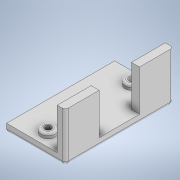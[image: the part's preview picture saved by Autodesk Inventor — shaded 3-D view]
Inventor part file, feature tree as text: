
AUTODESK INVENTOR PART (.ipt)
format: ipt  version: 2020 (Build 240168000, 168)  size: 183,296 bytes
history: native  units: in
note: dims shown in document units (in); Inventor stores cm internally (conversion verified against a paired STEP export)
features: extrude x5, sketch x4, fillet x2
ambient origin geometry x8: Origin, YZ Plane, XZ Plane, XY Plane, X Axis, Y Axis, Z Axis, Center Point
bodies: Solid1 (feature_tree)
feature tree (11):
  extrude  "Extrusion1"  Depth=2.6378in
  extrude  "Extrusion2"  Depth=0.1969in
  extrude  "Extrusion3"  Depth=0.1969in
  extrude  "Extrusion4"  Depth=1.0in TaperAngle=0.0deg
  extrude  "Extrusion5"  Depth=0.0197in
  fillet  "Fillet1"  Radius=0.3346in
  fillet  "Fillet2"  Radius=0.3346in
  sketch  "Sketch1"  dims[d0=1.4331in d1=2.6378in]
  sketch  "Sketch2"  dims[d2=0.1969in d3=0.0in d4=0.1969in]
  sketch  "Sketch3"  dims[d5=0.8268in d6=0.1969in]
  sketch  "Sketch4"  dims[d7=0.8268in d8=1.0in d9=0.0in d10=0.3346in d11=0.3346in d12=0.3346in d13=0.1181in d14=0.0in d15=0.2362in d16=0.2362in d17=0.1181in d18=0.0in d19=0.1575in d21=0.1575in d22=0.5906in d23=0.0in d24=0.0591in d25=0.0787in d26=0.7165in d27=0.7165in d30=0.1575in d31=0.0344in d32=0.0197in d33=0.0344in]
